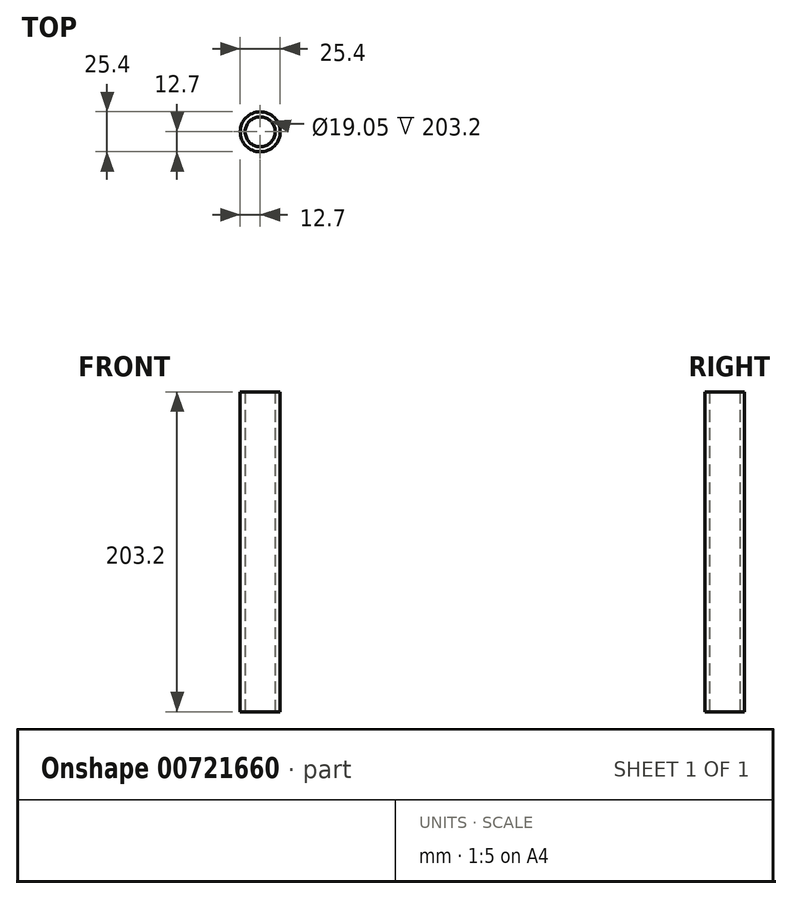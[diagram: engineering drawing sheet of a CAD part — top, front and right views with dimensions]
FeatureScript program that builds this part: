
annotation { "Feature Type Name" : "Feature", "Feature Type Description" : "" }
export const myFeature = defineFeature(function(context is Context, id is Id, definition is map)
    precondition{}
    {
        {
            var Q0;
            Q0=qCreatedBy(makeId("Top.planeOp"),FACE);
            var sketch = newSketch(context, id + "F0", { "sketchPlane" : qUnion([Q0])});
            skCircle(sketch, "E0", {"center": v(0, 0) * mm, "radius": 12.7 * mm});
            skCircle(sketch, "E1.0", {"center": v(0, 0) * mm, "radius": 9.53 * mm});
            skSolve(sketch);
        }
        {
            var Q0;
            Q0 = qSketchRegion(id + "F0", true);
            extrude(context, id + "F1", {"entities" : qUnion([Q0]), "depth" : 203.2 * mm, "offsetDistance" : 25.4 * mm});
        }
    });
